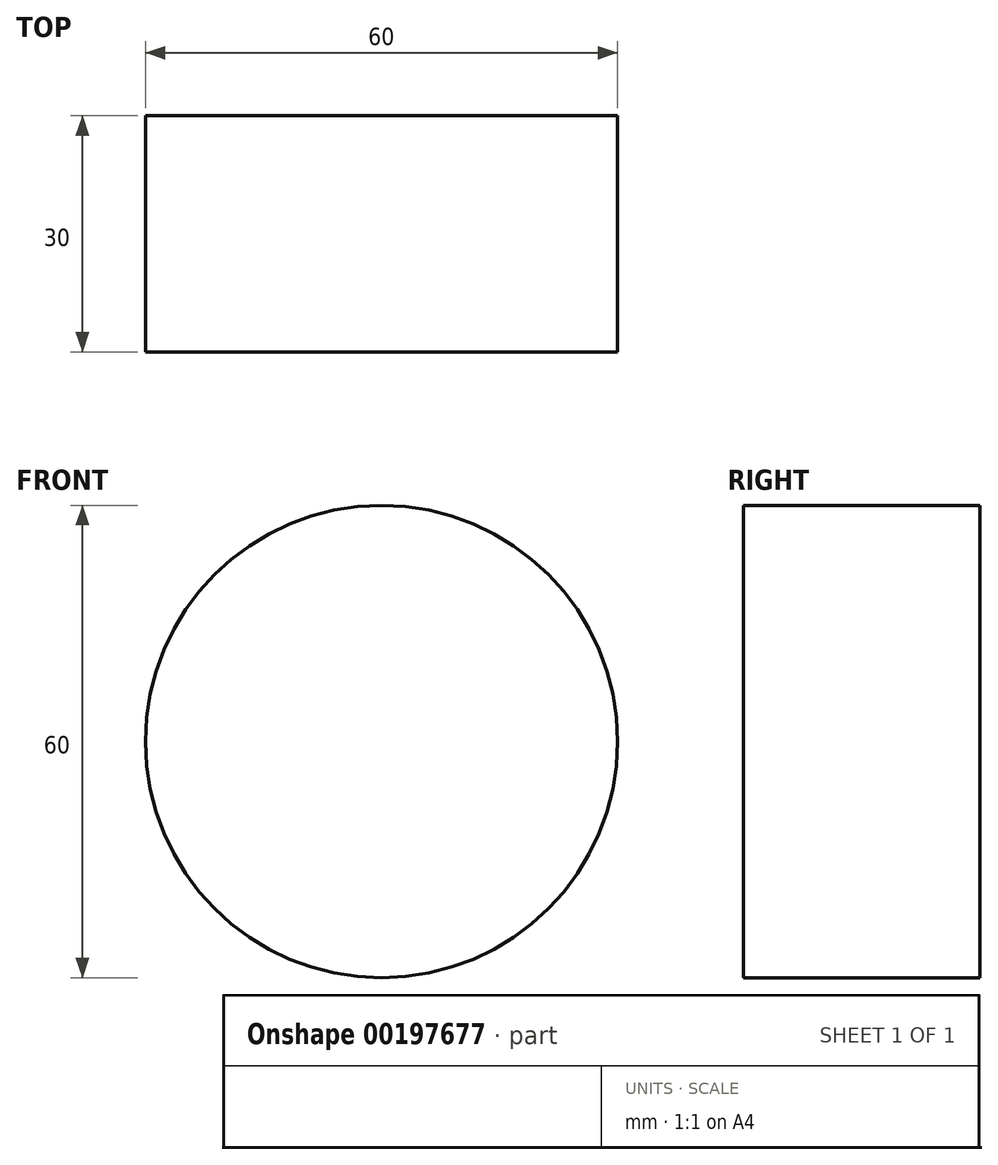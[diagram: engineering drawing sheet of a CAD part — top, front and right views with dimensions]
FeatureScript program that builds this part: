
annotation { "Feature Type Name" : "Feature", "Feature Type Description" : "" }
export const myFeature = defineFeature(function(context is Context, id is Id, definition is map)
    precondition{}
    {
        {
            var Q0;
            Q0=qCreatedBy(makeId("Front.planeOp"),FACE);
            var sketch = newSketch(context, id + "F0", { "sketchPlane" : qUnion([Q0])});
            skCircle(sketch, "E0", {"center": v(0, 0) * mm, "radius": 30 * mm});
            skSolve(sketch);
        }
        {
            var Q0;
            Q0 = qSketchRegion(id + "F0", true);
            extrude(context, id + "F1", {"entities" : qUnion([Q0]), "depth" : 30 * mm});
        }
    });
